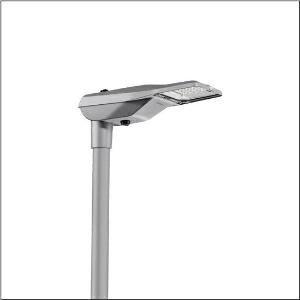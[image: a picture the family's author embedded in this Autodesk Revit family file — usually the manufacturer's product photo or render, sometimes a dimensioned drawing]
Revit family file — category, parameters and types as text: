
# Revit family: streetlight_sl_21_micro___st1_0a_5xe1d33t08db_ddb2
name_source: partatom
category: Lighting Fixtures
units: mm (PartAtom-declared; Revit-internal decimal feet)

## family parameters
Cut with Voids When Loaded = No
Host = Face
Light Source = No
Part Type = Normal
Room Calculation Point = No
Round Connector Dimension = Use Diameter
Shared = No

## types (1)
- --- (1 x LED, 5110 lm, 39.1 W, 3000K)
    Apparent Load = 39 VA
    CIE Flux Codes = 37 72 97 100 100
    Color Rendering = 70
    Color Temperature = 3000K
    Default Elevation = 1800 mm
    Description = Streetlight SL 21 micro, mast luminaire, primary light control with lens, of PMMA, primary optical cover: cover, of toughened safety glass, transparent, light distribution: ST1.0a, light emission: direct distribution, primary light characteristic: asymmetric, installation type: side-entry, post-top, LED, High Power LED, rated luminous flux: 5.110lm, luminous efficacy: 131lm/W, light colour: 730, colour temperature: 3000K, control: flexible luminous flux parameterisation, time-dependent luminous flux control, constant luminous flux control, overheat protection, pre-setting: logarithmic dimming characteristic, mains connection: 220..240V, AC, 50/60Hz, start of lifetime: 39W, end of service life: 41W, reduction: 18W, luminaire housing, of diecast aluminium, powder-coated, Siteco® metallic grey (DB 702S), corrosivity category C5 mid according to DIN EN ISO 12944, please order mast flange separately, inclination adjustable: 0°, 5°, 10°, 15°, sealing non-destructively replaceable, multi-level sealing system, length: 528mm, width: 235mm, height: 110mm, mast flange for spigot size: 42mm (side-entry): 5XC10008XM4, 60/48mm (side-entry/post-top): 5XC10108XM2, 76/60mm (side-entry/post-top): 5XC10108XM1, Smart Interface below and above, protection rating (complete): IP66, insulation class (complete): insulation class II (safety insulation), certification: CE, ENEC, ENEC+, VDE, impact resistance: IK09, permissible operating ambient temperature for outdoor applications: -40..+50°C, standard-compliant lighting for roads and squares, packaging unit: 1 piece

Light Distribution: ST1.0a
    Height = 110 mm
    Lamp = 1 x LED
    Lamp Light Flux = 5110 lm
    Lamp Power = 39.1 W
    Lamp count = 1
    Length = 528 mm
    Luminous efficacy = 131 lm/W
    Manufacturer = Siteco
    ModVariant = No
    Model = 5XE1D33T08DB
    Number of Poles = 1
    OnlyDefault = Yes
    Power Factor = 1
    Product Name = Streetlight SL 21 micro | ST1.0a
    Product group = mast luminaire | pylon top
    ProductGroupID = 6100
    Protection Class = Protection class II
    Protection Degree = IP 66
    RLX_Detail_Level = 1
    RLX_Emergency_Light_Flux = 0 lm
    RLX_Emergency_Type = 0
    RLX_Emergency_Type_DB = No
    RlxData = <blob elided: 98709 chars, md5=b58058c2>
    Socket = socket
    Standby Power = 0 W
    System Light Flux = 5110 lm
    System Power = 39 W
    Type Comments = factory setting: luminous flux: 100 % | dim-lin: 254 | 765 mA
    Type Image = l_1007239.jpg
    URL = http://relux.com
    VarID = @adj_126131
    Voltage = 0 V
    Weight = 0.00 kg
    Width = 235 mm

## geometry (parser evidence)
native form markers: Blend x4, Sweep x12
no freeform markers — native parametric forms only
